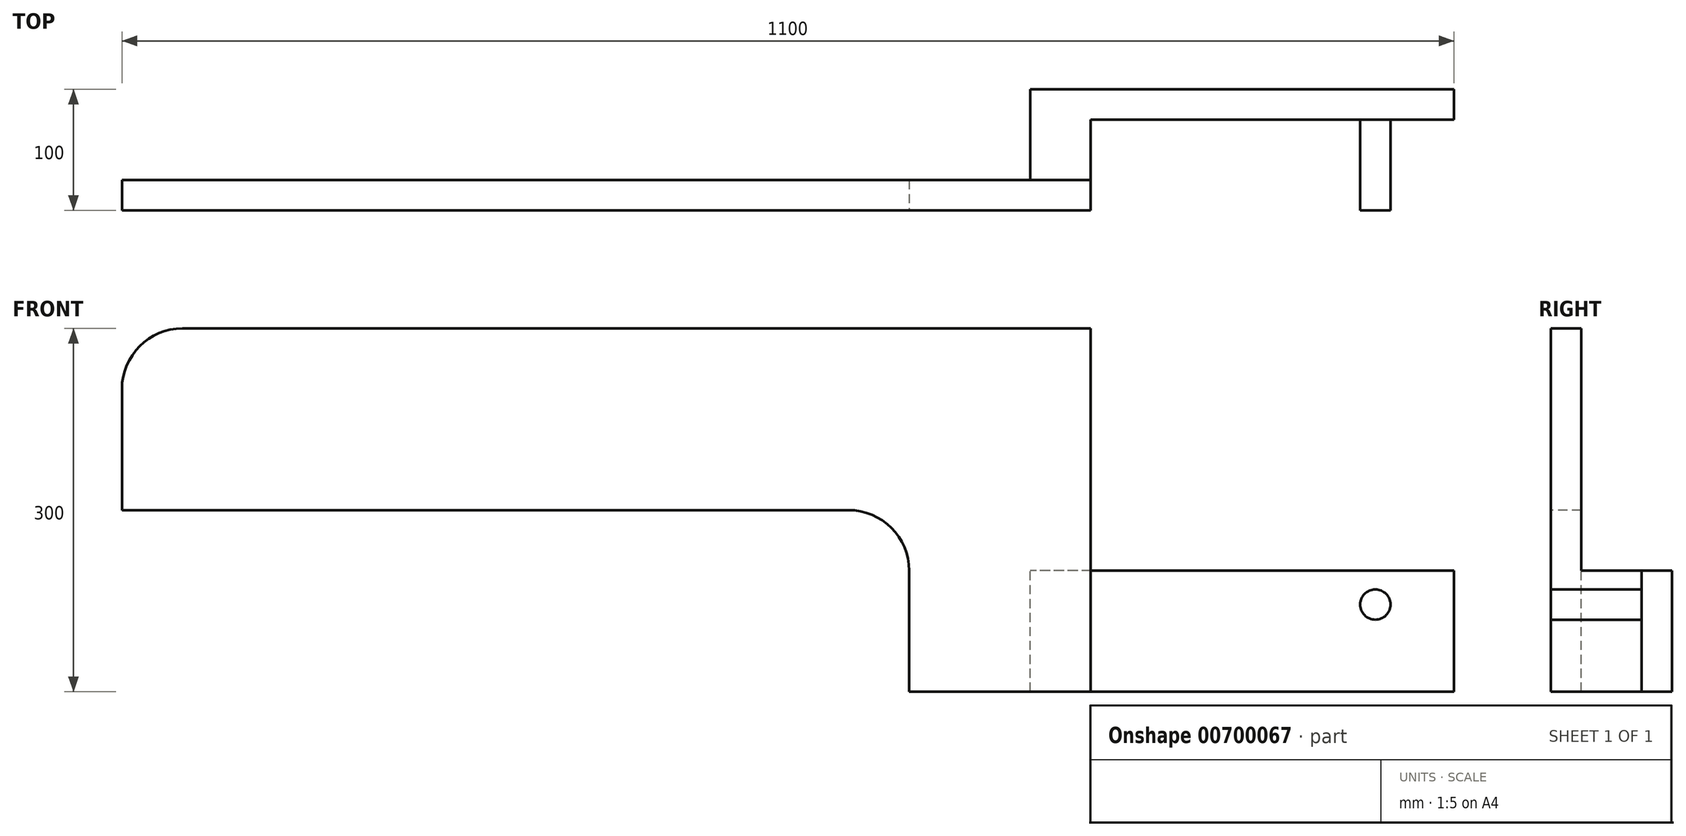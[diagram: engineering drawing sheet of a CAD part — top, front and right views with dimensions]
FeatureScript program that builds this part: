
annotation { "Feature Type Name" : "Feature", "Feature Type Description" : "" }
export const myFeature = defineFeature(function(context is Context, id is Id, definition is map)
    precondition{}
    {
        {
            var Q0;
            Q0=qCreatedBy(makeId("Front.planeOp"),FACE);
            var sketch = newSketch(context, id + "F0", { "sketchPlane" : qUnion([Q0])});
            skLineSegment(sketch, "E0.bottom", {"start": v(400, 150) * mm, "end": v(-400, 150) * mm});
            skLineSegment(sketch, "E0.top", {"start": v(400, -150) * mm, "end": v(-400, -150) * mm});
            skLineSegment(sketch, "E0.left", {"start": v(400, 150) * mm, "end": v(400, -150) * mm});
            skLineSegment(sketch, "E0.right", {"start": v(-400, 150) * mm, "end": v(-400, -150) * mm});
            skPoint(sketch, "E0.middle", {"position": v(0, 0) * mm});
            skSolve(sketch);
        }
        {
            var Q0;
            Q0=makeQuery(id+"F0.imprint","IMPRINT",FACE,{"disambiguationData":[TD([[makeQuery(id+"F0.imprint","IMPRINT",EDGE,{"derivedFrom":sQuery(id+"F0.wireOp",EDGE,"E0.bottom")}),1.0]])]});
            extrude(context, id + "F1", {"entities" : qUnion([Q0]), "depth" : 25 * mm, "offsetDistance" : 25 * mm});
        }
        {
            var Q0;
            Q0=makeQuery(id+"F1.opExtrude","CAP_FACE",FACE,{"disambiguationData":[OSD([sQuery(id+"F0.wireOp",EDGE,"E0.bottom"),sQuery(id+"F0.wireOp",EDGE,"E0.top"),sQuery(id+"F0.wireOp",EDGE,"E0.left"),sQuery(id+"F0.wireOp",EDGE,"E0.right")])],"isStart":true});
            var sketch = newSketch(context, id + "F2", { "sketchPlane" : qUnion([Q0])});
            skLineSegment(sketch, "E1.bottom", {"start": v(-400, -150) * mm, "end": v(-350, -150) * mm});
            skLineSegment(sketch, "E1.top", {"start": v(-400, -50) * mm, "end": v(-350, -50) * mm});
            skLineSegment(sketch, "E1.left", {"start": v(-400, -150) * mm, "end": v(-400, -50) * mm});
            skLineSegment(sketch, "E1.right", {"start": v(-350, -150) * mm, "end": v(-350, -50) * mm});
            skSolve(sketch);
        }
        {
            var Q0;
            Q0=makeQuery(id+"F2.imprint","IMPRINT",FACE,{"disambiguationData":[TD([[makeQuery(id+"F2.imprint","IMPRINT",EDGE,{"derivedFrom":sQuery(id+"F2.wireOp",EDGE,"E1.bottom")}),1.0]])]});
            extrude(context, id + "F3", {"entities" : qUnion([Q0]), "operationType" : NewBodyOperationType.ADD, "depth" : 75 * mm, "offsetDistance" : 25 * mm});
        }
        {
            var Q0;
            Q0=makeQuery(id+"F3.boolean.opBoolean","MERGE",FACE,{"derivedFrom":[makeQuery(id+"F1.opExtrude","SWEPT_FACE",FACE,{"disambiguationData":[OSD([sQuery(id+"F0.wireOp",EDGE,"E0.left")])]}),makeQuery(id+"F3.opExtrude","SWEPT_FACE",FACE,{"disambiguationData":[OSD([sQuery(id+"F2.wireOp",EDGE,"E1.left")])]})]});
            var sketch = newSketch(context, id + "F4", { "sketchPlane" : qUnion([Q0])});
            skLineSegment(sketch, "E2.bottom", {"start": v(75, -50) * mm, "end": v(50, -50) * mm});
            skLineSegment(sketch, "E2.top", {"start": v(75, -150) * mm, "end": v(50, -150) * mm});
            skLineSegment(sketch, "E2.left", {"start": v(75, -50) * mm, "end": v(75, -150) * mm});
            skLineSegment(sketch, "E2.right", {"start": v(50, -50) * mm, "end": v(50, -150) * mm});
            skSolve(sketch);
        }
        {
            var Q0;
            Q0=makeQuery(id+"F4.imprint","IMPRINT",FACE,{"disambiguationData":[TD([[makeQuery(id+"F4.imprint","IMPRINT",EDGE,{"derivedFrom":sQuery(id+"F4.wireOp",EDGE,"E2.bottom")}),1.0]])]});
            extrude(context, id + "F5", {"entities" : qUnion([Q0]), "operationType" : NewBodyOperationType.ADD, "depth" : 300 * mm, "offsetDistance" : 25 * mm});
        }
        {
            var Q0;
            Q0=makeQuery(id+"F5.opExtrude","SWEPT_FACE",FACE,{"disambiguationData":[OSD([sQuery(id+"F4.wireOp",EDGE,"E2.right")])]});
            var sketch = newSketch(context, id + "F6", { "sketchPlane" : qUnion([Q0])});
            skCircle(sketch, "E3", {"center": v(635, -78) * mm, "radius": 12.5 * mm});
            skSolve(sketch);
        }
        {
            var Q0;
            Q0=makeQuery(id+"F6.imprint","IMPRINT",FACE,{"disambiguationData":[TD([[makeQuery(id+"F6.imprint","IMPRINT",EDGE,{"derivedFrom":sQuery(id+"F6.wireOp",EDGE,"E3")}),1.0]])]});
            extrude(context, id + "F7", {"entities" : qUnion([Q0]), "operationType" : NewBodyOperationType.ADD, "depth" : 75 * mm, "offsetDistance" : 25 * mm});
        }
        {
            var Q0;
            Q0=makeQuery(id+"F1.opExtrude","CAP_FACE",FACE,{"disambiguationData":[OSD([sQuery(id+"F0.wireOp",EDGE,"E0.bottom"),sQuery(id+"F0.wireOp",EDGE,"E0.top"),sQuery(id+"F0.wireOp",EDGE,"E0.left"),sQuery(id+"F0.wireOp",EDGE,"E0.right")])],"isStart":false});
            var sketch = newSketch(context, id + "F8", { "sketchPlane" : qUnion([Q0])});
            skPoint(sketch, "E4.oppositeSnap0", {"position": v(-400, 0) * mm});
            skLineSegment(sketch, "E4.bottom", {"start": v(-400, -150) * mm, "end": v(250, -150) * mm});
            skLineSegment(sketch, "E4.top", {"start": v(-400, 0) * mm, "end": v(250, 0) * mm});
            skLineSegment(sketch, "E4.left", {"start": v(-400, -150) * mm, "end": v(-400, 0) * mm});
            skLineSegment(sketch, "E4.right", {"start": v(250, -150) * mm, "end": v(250, 0) * mm});
            skSolve(sketch);
        }
        {
            var Q0;
            Q0=makeQuery(id+"F8.imprint","IMPRINT",FACE,{"disambiguationData":[TD([[makeQuery(id+"F8.imprint","IMPRINT",EDGE,{"derivedFrom":sQuery(id+"F8.wireOp",EDGE,"E4.bottom")}),-1.0]])]});
            extrude(context, id + "F9", {"entities" : qUnion([Q0]), "operationType" : NewBodyOperationType.REMOVE, "oppositeDirection" : true, "depth" : 25 * mm, "offsetDistance" : 25 * mm});
        }
        {
            var Q0;
            Q0=makeQuery(id+"F9.boolean.opBoolean","COPY",EDGE,{"derivedFrom":makeQuery(id+"F9.opExtrude","SWEPT_EDGE",EDGE,{"disambiguationData":[OSD([sQuery(id+"F0.wireOp",EDGE,"E0.right"),sQuery(id+"F8.wireOp",EDGE,"E4.top"),sQuery(id+"F8.wireOp",EDGE,"E4.left")])]})});
            var Q1;
            Q1=makeQuery(id+"F9.boolean.opBoolean","COPY",EDGE,{"derivedFrom":makeQuery(id+"F9.opExtrude","SWEPT_EDGE",EDGE,{"disambiguationData":[OSD([sQuery(id+"F8.wireOp",EDGE,"E4.top"),sQuery(id+"F8.wireOp",EDGE,"E4.right")])]})});
            var Q2;
            Q2=makeQuery(id+"F9.boolean.opBoolean","COPY",EDGE,{"derivedFrom":makeQuery(id+"F9.opExtrude","SWEPT_EDGE",EDGE,{"disambiguationData":[OSD([sQuery(id+"F0.wireOp",EDGE,"E0.top"),sQuery(id+"F8.wireOp",EDGE,"E4.bottom"),sQuery(id+"F8.wireOp",EDGE,"E4.right")])]})});
            fillet(context, id + "F10", {"entities" : qUnion([Q0, Q1, Q2]), "radius" : 50 * mm, "tangentPropagation" : true, "allowEdgeOverflow" : false});
        }
        {
            var Q0;
            Q0=makeQuery(id+"F1.opExtrude","SWEPT_EDGE",EDGE,{"disambiguationData":[OSD([sQuery(id+"F0.wireOp",EDGE,"E0.bottom"),sQuery(id+"F0.wireOp",EDGE,"E0.right")])]});
            fillet(context, id + "F11", {"entities" : qUnion([Q0]), "radius" : 50 * mm, "tangentPropagation" : true, "allowEdgeOverflow" : false});
        }
    });
